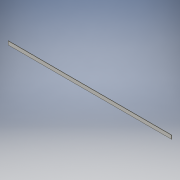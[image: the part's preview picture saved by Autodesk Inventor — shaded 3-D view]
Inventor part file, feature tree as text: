
AUTODESK INVENTOR PART (.ipt)
format: ipt  version: 2018 (Build 220112000, 112)  size: 94,208 bytes
history: native  units: mm
features: extrude x1, sketch x1
ambient origin geometry x8: Origin, YZ Plane, XZ Plane, XY Plane, X Axis, Y Axis, Z Axis, Center Point
bodies: Solid1 (feature_tree)
feature tree (2):
  extrude  "Extrusion1"  Depth=30.0mm
  sketch  "Sketch1"  dims[d0=1400.0mm d1=30.0mm d2=2.5mm d3=0.0mm]
